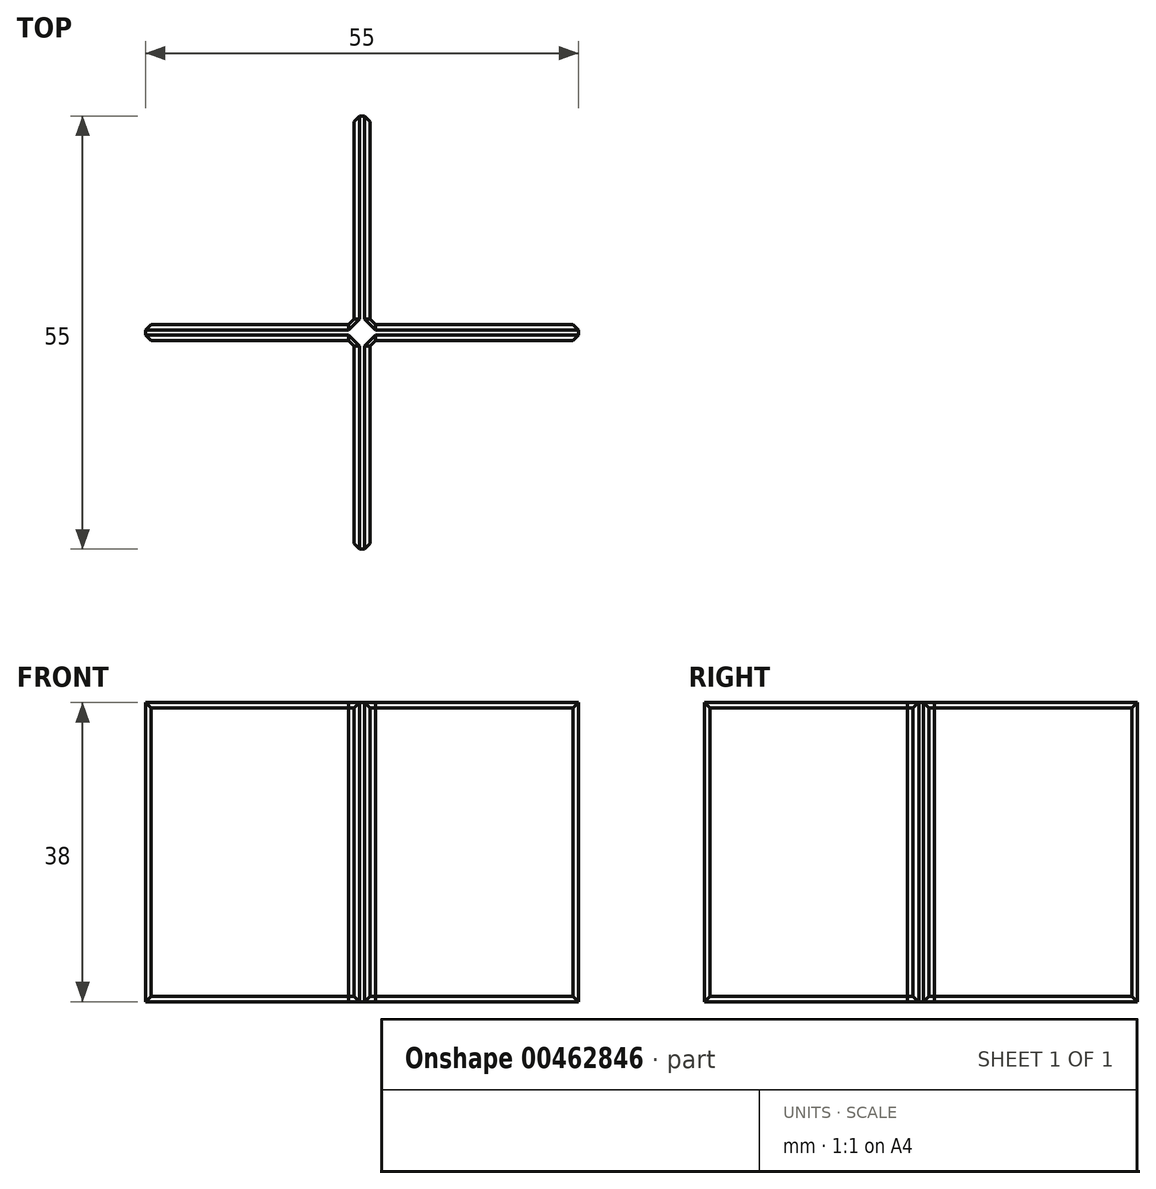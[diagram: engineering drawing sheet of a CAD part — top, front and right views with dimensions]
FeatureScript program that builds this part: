
annotation { "Feature Type Name" : "Feature", "Feature Type Description" : "" }
export const myFeature = defineFeature(function(context is Context, id is Id, definition is map)
    precondition{}
    {
        {
            var Q0;
            Q0=qCreatedBy(makeId("Top.planeOp"),FACE);
            var sketch = newSketch(context, id + "F0", { "sketchPlane" : qUnion([Q0])});
            skLineSegment(sketch, "E0.bottom", {"start": v(0, 0) * mm, "end": v(-2, 0) * mm});
            skLineSegment(sketch, "E0.top", {"start": v(0, 55) * mm, "end": v(-2, 55) * mm});
            skLineSegment(sketch, "E0.left", {"start": v(0, 0) * mm, "end": v(0, 55) * mm});
            skLineSegment(sketch, "E0.right", {"start": v(-2, 0) * mm, "end": v(-2, 55) * mm});
            skLineSegment(sketch, "E1", {"start": v(0, 0) * mm, "end": v(13.96, 0) * mm});
            skLineSegment(sketch, "E2", {"start": v(18.5, 0) * mm, "end": v(26.01, 0) * mm});
            skSolve(sketch);
        }
        {
            var Q0;
            Q0=makeQuery(id+"F0.imprint","IMPRINT",FACE,{"disambiguationData":[TD([[makeQuery(id+"F0.imprint","IMPRINT",EDGE,{"derivedFrom":sQuery(id+"F0.wireOp",EDGE,"E0.bottom")}),-1.0]])]});
            extrude(context, id + "F1", {"entities" : qUnion([Q0]), "depth" : 38 * mm});
        }
        {
            var Q0;
            Q0=qCreatedBy(makeId("Top.planeOp"),FACE);
            var sketch = newSketch(context, id + "F2", { "sketchPlane" : qUnion([Q0])});
            skLineSegment(sketch, "E3", {"start": v(13.67, 0) * mm, "end": v(36.23, 0) * mm});
            skSolve(sketch);
        }
        {
            var Q0;
            Q0=makeQuery(id+"F1.opExtrude","SWEPT_BODY",BODY,{"disambiguationData":[OSD([sQuery(id+"F0.wireOp",EDGE,"E0.bottom"),sQuery(id+"F0.wireOp",EDGE,"E0.top"),sQuery(id+"F0.wireOp",EDGE,"E0.left"),sQuery(id+"F0.wireOp",EDGE,"E0.right")])]});
            var Q1;
            Q1=sQuery(id+"F2.wireOp",EDGE,"E3");
            transform(context, id + "F3", {"entities" : qUnion([Q0]), "transformType" : TransformType.TRANSLATION_DISTANCE, "transformDirection" : qUnion([Q1]), "distance" : 1 * mm, "makeCopy" : false});
        }
        {
            var Q0;
            Q0=qCreatedBy(makeId("Top.planeOp"),FACE);
            var sketch = newSketch(context, id + "F4", { "sketchPlane" : qUnion([Q0])});
            skLineSegment(sketch, "E4", {"start": v(0, 62.06) * mm, "end": v(0, 72.35) * mm});
            skSolve(sketch);
        }
        {
            var Q0;
            Q0=makeQuery(id+"F1.opExtrude","SWEPT_BODY",BODY,{"disambiguationData":[OSD([sQuery(id+"F0.wireOp",EDGE,"E0.bottom"),sQuery(id+"F0.wireOp",EDGE,"E0.top"),sQuery(id+"F0.wireOp",EDGE,"E0.left"),sQuery(id+"F0.wireOp",EDGE,"E0.right")])]});
            var Q1;
            Q1=sQuery(id+"F4.wireOp",EDGE,"E4");
            transform(context, id + "F5", {"entities" : qUnion([Q0]), "transformType" : TransformType.TRANSLATION_DISTANCE, "transformDirection" : qUnion([Q1]), "distance" : 27.5 * mm, "oppositeDirection" : true, "makeCopy" : false});
        }
        {
            var Q0;
            Q0=qCreatedBy(makeId("Front.planeOp"),FACE);
            var sketch = newSketch(context, id + "F6", { "sketchPlane" : qUnion([Q0])});
            skLineSegment(sketch, "E5", {"start": v(0, 0) * mm, "end": v(0, 58.5) * mm});
            skSolve(sketch);
        }
        {
            var Q0;
            Q0=makeQuery(id+"F1.opExtrude","SWEPT_BODY",BODY,{"disambiguationData":[OSD([sQuery(id+"F0.wireOp",EDGE,"E0.bottom"),sQuery(id+"F0.wireOp",EDGE,"E0.top"),sQuery(id+"F0.wireOp",EDGE,"E0.left"),sQuery(id+"F0.wireOp",EDGE,"E0.right")])]});
            var Q1;
            Q1=sQuery(id+"F6.wireOp",EDGE,"E5");
            circularPattern(context, id + "F7", {"entities" : qUnion([Q0]), "axis" : qUnion([Q1]), "angle" : 360 * degree, "instanceCount" : 4, "equalSpace" : true});
        }
        {
            var Q0;
            Q0=makeQuery(id+"F1.opExtrude","SWEPT_BODY",BODY,{"disambiguationData":[OSD([sQuery(id+"F0.wireOp",EDGE,"E0.bottom"),sQuery(id+"F0.wireOp",EDGE,"E0.top"),sQuery(id+"F0.wireOp",EDGE,"E0.left"),sQuery(id+"F0.wireOp",EDGE,"E0.right")])]});
            var Q1;
            Q1=makeQuery(id+"F7.opPattern","COPY",BODY,{"derivedFrom":makeQuery(id+"F1.opExtrude","SWEPT_BODY",BODY,{"disambiguationData":[OSD([sQuery(id+"F0.wireOp",EDGE,"E0.bottom"),sQuery(id+"F0.wireOp",EDGE,"E0.top"),sQuery(id+"F0.wireOp",EDGE,"E0.left"),sQuery(id+"F0.wireOp",EDGE,"E0.right")])]}),"instanceName":"1"});
            var Q2;
            Q2=makeQuery(id+"F7.opPattern","COPY",BODY,{"derivedFrom":makeQuery(id+"F1.opExtrude","SWEPT_BODY",BODY,{"disambiguationData":[OSD([sQuery(id+"F0.wireOp",EDGE,"E0.bottom"),sQuery(id+"F0.wireOp",EDGE,"E0.top"),sQuery(id+"F0.wireOp",EDGE,"E0.left"),sQuery(id+"F0.wireOp",EDGE,"E0.right")])]}),"instanceName":"2"});
            var Q3;
            Q3=makeQuery(id+"F7.opPattern","COPY",BODY,{"derivedFrom":makeQuery(id+"F1.opExtrude","SWEPT_BODY",BODY,{"disambiguationData":[OSD([sQuery(id+"F0.wireOp",EDGE,"E0.bottom"),sQuery(id+"F0.wireOp",EDGE,"E0.top"),sQuery(id+"F0.wireOp",EDGE,"E0.left"),sQuery(id+"F0.wireOp",EDGE,"E0.right")])]}),"instanceName":"3"});
            booleanBodies(context, id + "F8", {"operationType" : BooleanOperationType.UNION, "tools" : qUnion([Q0, Q1, Q2, Q3])});
        }
        {
            var Q0;
            {var subQ0=sQuery(id+"F0.wireOp",EDGE,"E0.left");var subQ1=makeQuery(id+"F1.opExtrude","SWEPT_FACE",FACE,{"disambiguationData":[OSD([subQ0])]});Q0=makeQuery(id+"F8.opBoolean","SPLIT",FACE,{"disambiguationData":[TD([subQ1])],"derivedFrom":makeQuery(id+"F7.opPattern","COPY",FACE,{"derivedFrom":subQ1,"instanceName":"1"})});}
            var Q1;
            {var subQ0=sQuery(id+"F0.wireOp",EDGE,"E0.top");var subQ2=sQuery(id+"F0.wireOp",EDGE,"E0.left");var subQ6=makeQuery(id+"F1.opExtrude","SWEPT_FACE",FACE,{"disambiguationData":[OSD([subQ2])]});Q1=makeQuery(id+"F8.opBoolean","SPLIT",FACE,{"disambiguationData":[TD([makeQuery(id+"F1.opExtrude","SWEPT_FACE",FACE,{"disambiguationData":[OSD([subQ0])]})])],"derivedFrom":subQ6});}
            var Q2;
            {var subQ0=sQuery(id+"F0.wireOp",EDGE,"E0.right");var subQ2=sQuery(id+"F0.wireOp",EDGE,"E0.left");Q2=makeQuery(id+"F8.opBoolean","SPLIT",FACE,{"disambiguationData":[TD([makeQuery(id+"F1.opExtrude","SWEPT_FACE",FACE,{"disambiguationData":[OSD([subQ0])]})])],"derivedFrom":makeQuery(id+"F7.opPattern","COPY",FACE,{"derivedFrom":makeQuery(id+"F1.opExtrude","SWEPT_FACE",FACE,{"disambiguationData":[OSD([subQ2])]}),"instanceName":"1"})});}
            var Q3;
            {var subQ0=sQuery(id+"F0.wireOp",EDGE,"E0.top");var subQ1=sQuery(id+"F0.wireOp",EDGE,"E0.right");Q3=makeQuery(id+"F8.opBoolean","SPLIT",FACE,{"disambiguationData":[TD([makeQuery(id+"F1.opExtrude","SWEPT_FACE",FACE,{"disambiguationData":[OSD([subQ0])]})])],"derivedFrom":makeQuery(id+"F1.opExtrude","SWEPT_FACE",FACE,{"disambiguationData":[OSD([subQ1])]})});}
            var Q4;
            {var subQ0=sQuery(id+"F0.wireOp",EDGE,"E0.right");var subQ3=sQuery(id+"F0.wireOp",EDGE,"E0.bottom");var subQ6=makeQuery(id+"F1.opExtrude","SWEPT_FACE",FACE,{"disambiguationData":[OSD([subQ0])]});Q4=makeQuery(id+"F8.opBoolean","SPLIT",FACE,{"disambiguationData":[TD([makeQuery(id+"F1.opExtrude","SWEPT_FACE",FACE,{"disambiguationData":[OSD([subQ3])]})])],"derivedFrom":subQ6});}
            var Q5;
            {var subQ0=sQuery(id+"F0.wireOp",EDGE,"E0.right");var subQ1=makeQuery(id+"F1.opExtrude","SWEPT_FACE",FACE,{"disambiguationData":[OSD([subQ0])]});Q5=makeQuery(id+"F8.opBoolean","SPLIT",FACE,{"disambiguationData":[TD([subQ1])],"derivedFrom":makeQuery(id+"F7.opPattern","COPY",FACE,{"derivedFrom":subQ1,"instanceName":"1"})});}
            var Q6;
            {var subQ1=sQuery(id+"F0.wireOp",EDGE,"E0.left");var subQ3=sQuery(id+"F0.wireOp",EDGE,"E0.bottom");Q6=makeQuery(id+"F8.opBoolean","SPLIT",FACE,{"disambiguationData":[TD([makeQuery(id+"F1.opExtrude","SWEPT_FACE",FACE,{"disambiguationData":[OSD([subQ3])]})])],"derivedFrom":makeQuery(id+"F1.opExtrude","SWEPT_FACE",FACE,{"disambiguationData":[OSD([subQ1])]})});}
            var Q7;
            {var subQ0=sQuery(id+"F0.wireOp",EDGE,"E0.left");var subQ1=sQuery(id+"F0.wireOp",EDGE,"E0.right");Q7=makeQuery(id+"F8.opBoolean","SPLIT",FACE,{"disambiguationData":[TD([makeQuery(id+"F1.opExtrude","SWEPT_FACE",FACE,{"disambiguationData":[OSD([subQ0])]})])],"derivedFrom":makeQuery(id+"F7.opPattern","COPY",FACE,{"derivedFrom":makeQuery(id+"F1.opExtrude","SWEPT_FACE",FACE,{"disambiguationData":[OSD([subQ1])]}),"instanceName":"1"})});}
            chamfer(context, id + "F9", {"entities" : qUnion([Q0, Q1, Q2, Q3, Q4, Q5, Q6, Q7]), "width" : 0.7 * mm, "tangentPropagation" : true});
        }
    });
